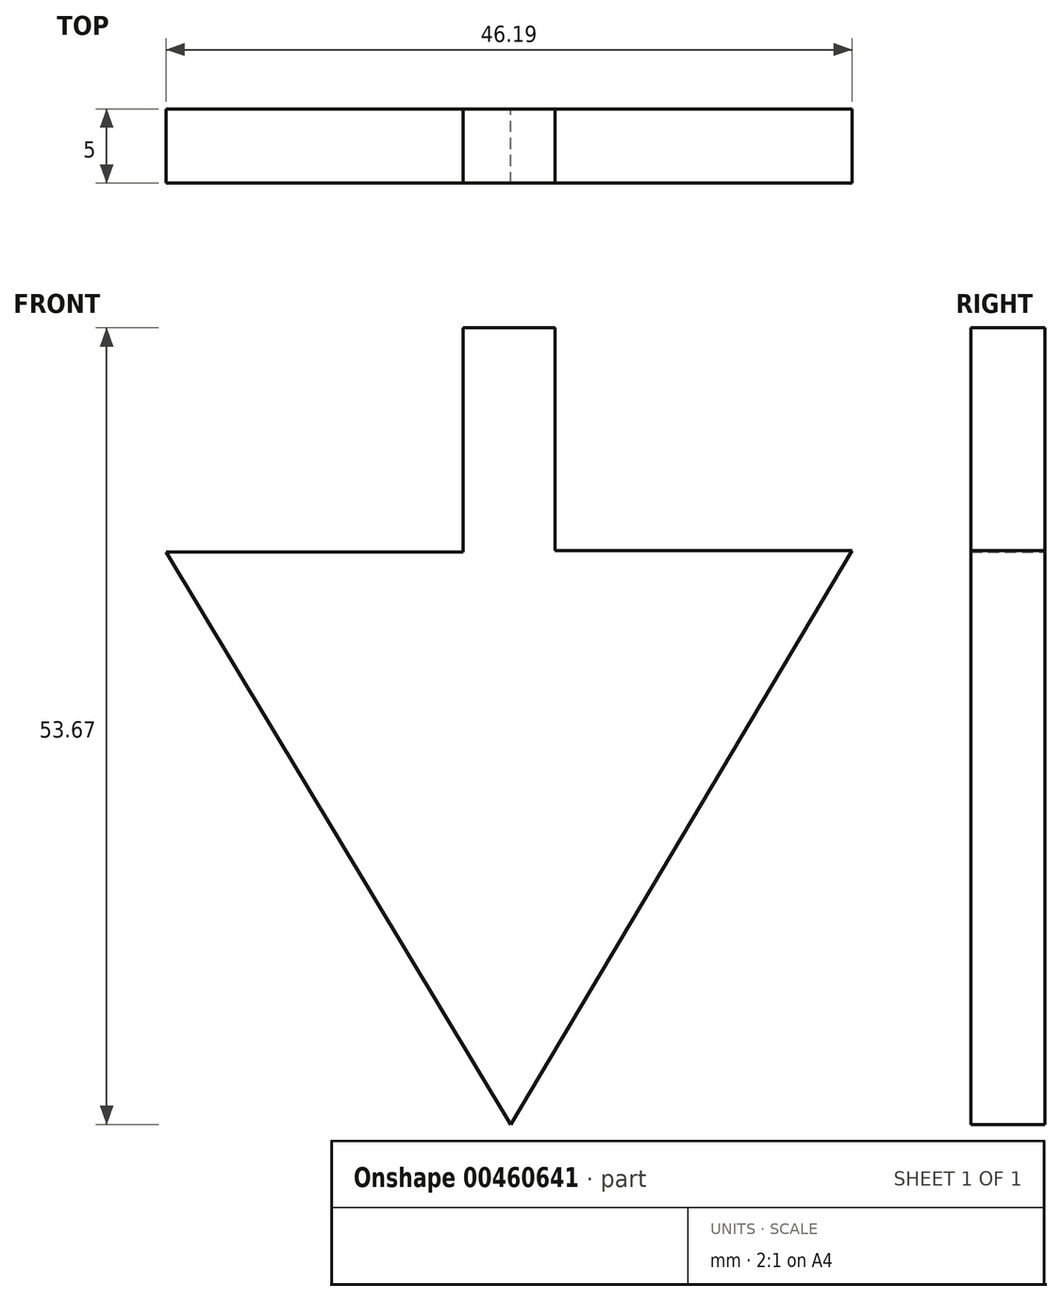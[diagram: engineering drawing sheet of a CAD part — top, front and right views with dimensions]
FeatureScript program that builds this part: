
annotation { "Feature Type Name" : "Feature", "Feature Type Description" : "" }
export const myFeature = defineFeature(function(context is Context, id is Id, definition is map)
    precondition{}
    {
        {
            var Q0;
            Q0=qCreatedBy(makeId("Front.planeOp"),FACE);
            var sketch = newSketch(context, id + "F0", { "sketchPlane" : qUnion([Q0])});
            skLineSegment(sketch, "E0", {"start": v(0, 49.14) * mm, "end": v(3, 49.14) * mm});
            skLineSegment(sketch, "E1", {"start": v(3, 49.14) * mm, "end": v(3, 34.14) * mm});
            skLineSegment(sketch, "E2", {"start": v(3, 34.14) * mm, "end": v(23, 34.14) * mm});
            skLineSegment(sketch, "E3", {"start": v(23, 34.14) * mm, "end": v(0, -4.53) * mm});
            skLineSegment(sketch, "E4", {"start": v(0, -4.53) * mm, "end": v(0, 49.14) * mm});
            skLineSegment(sketch, "E5", {"start": v(0, 49.14) * mm, "end": v(-3.2, 49.14) * mm});
            skLineSegment(sketch, "E6", {"start": v(-3.2, 49.14) * mm, "end": v(-3.2, 34.03) * mm});
            skLineSegment(sketch, "E7", {"start": v(-3.2, 34.03) * mm, "end": v(-23.2, 34.03) * mm});
            skLineSegment(sketch, "E8", {"start": v(-23.2, 34.03) * mm, "end": v(0, -4.53) * mm});
            skSolve(sketch);
        }
        {
            var Q0;
            Q0 = qSketchRegion(id + "F0", true);
            extrude(context, id + "F1", {"entities" : qUnion([Q0]), "depth" : 5 * mm});
        }
    });
